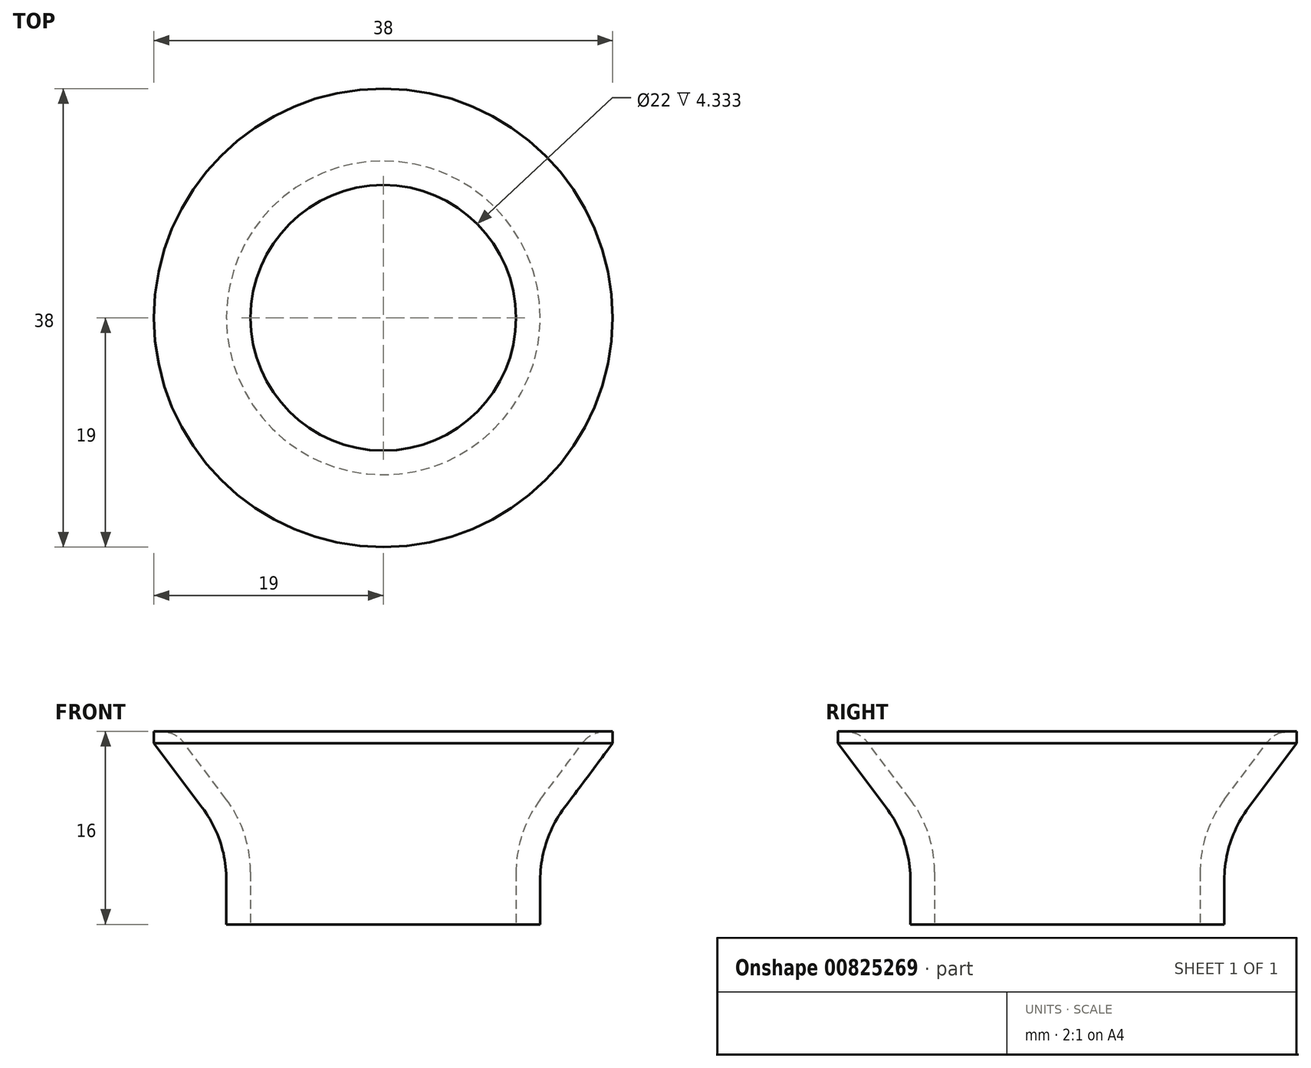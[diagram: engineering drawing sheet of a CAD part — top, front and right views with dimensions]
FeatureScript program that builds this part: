
annotation { "Feature Type Name" : "Feature", "Feature Type Description" : "" }
export const myFeature = defineFeature(function(context is Context, id is Id, definition is map)
    precondition{}
    {
        {
            var Q0;
            Q0=qCreatedBy(makeId("Top.planeOp"),FACE);
            var sketch = newSketch(context, id + "F0", { "sketchPlane" : qUnion([Q0])});
            skCircle(sketch, "E0", {"center": v(0, 0) * mm, "radius": 13 * mm});
            skSolve(sketch);
        }
        {
            var Q0;
            Q0=qCreatedBy(makeId("Top.planeOp"),FACE);
            cPlane(context, id + "F1", {"entities" : qUnion([Q0]), "cplaneType" : CPlaneType.OFFSET, "offset" : 15 * mm, "width" : 150 * mm, "height" : 150 * mm});
        }
        {
            var Q0;
            Q0=qCreatedBy(id+"F1.planeOp",FACE);
            var sketch = newSketch(context, id + "F2", { "sketchPlane" : qUnion([Q0])});
            skCircle(sketch, "E1", {"center": v(0, 0) * mm, "radius": 19 * mm});
            skSolve(sketch);
        }
        {
            var Q0;
            Q0=makeQuery(id+"F0.imprint","IMPRINT",FACE,{"disambiguationData":[TD([[makeQuery(id+"F0.imprint","IMPRINT",EDGE,{"derivedFrom":sQuery(id+"F0.wireOp",EDGE,"E0")}),1.0]])]});
            extrude(context, id + "F3", {"entities" : qUnion([Q0]), "depth" : 7 * mm, "offsetDistance" : 25 * mm});
        }
        {
            var Q0;
            Q0=makeQuery(id+"F2.imprint","IMPRINT",FACE,{"disambiguationData":[TD([[makeQuery(id+"F2.imprint","IMPRINT",EDGE,{"derivedFrom":sQuery(id+"F2.wireOp",EDGE,"E1")}),1.0]])]});
            extrude(context, id + "F4", {"entities" : qUnion([Q0]), "depth" : 1 * mm, "offsetDistance" : 25 * mm});
        }
        {
            var Q0;
            Q0=makeQuery(id+"F3.opExtrude","CAP_FACE",FACE,{"disambiguationData":[OSD([sQuery(id+"F0.wireOp",EDGE,"E0")])],"isStart":false});
            var Q1;
            Q1=makeQuery(id+"F4.opExtrude","CAP_FACE",FACE,{"disambiguationData":[OSD([sQuery(id+"F2.wireOp",EDGE,"E1")])],"isStart":true});
            loft(context, id + "F5", {"operationType" : NewBodyOperationType.ADD, "sheetProfilesArray" : [{ "sheetProfileEntities" : qUnion([Q0]) }, { "sheetProfileEntities" : qUnion([Q1]) }]});
        }
        {
            var Q0;
            Q0=makeQuery(id+"F4.opExtrude","CAP_FACE",FACE,{"disambiguationData":[OSD([sQuery(id+"F2.wireOp",EDGE,"E1")])],"isStart":false});
            var Q1;
            Q1=makeQuery(id+"F3.opExtrude","CAP_FACE",FACE,{"disambiguationData":[OSD([sQuery(id+"F0.wireOp",EDGE,"E0")])],"isStart":true});
            shell(context, id + "F6", {"entities" : qUnion([Q0, Q1]), "thickness" : 2 * mm});
        }
        {
            var Q0;
            {var subQ0=sQuery(id+"F0.wireOp",EDGE,"E0");Q0=makeQuery(id+"F5.boolean.opBoolean","MERGE",EDGE,{"derivedFrom":[makeQuery(id+"F3.opExtrude","CAP_EDGE",EDGE,{"disambiguationData":[OSD([subQ0])],"isStart":false}),makeQuery(id+"F5.opLoft","MID_CAP_EDGE",EDGE,{"disambiguationData":[OSD([subQ0])],"capPos":0.0})]});}
            fillet(context, id + "F7", {"entities" : qUnion([Q0]), "radius" : 10 * mm, "tangentPropagation" : true, "allowEdgeOverflow" : false});
        }
        {
            var Q0;
            {var subQ0=sQuery(id+"F2.wireOp",EDGE,"E1");Q0=makeQuery(id+"F6.opShell","OFFSET_EDGE",EDGE,{"disambiguationData":[OSD([subQ0]),TDD([makeQuery(id+"F4.opExtrude","CAP_EDGE",EDGE,{"disambiguationData":[OSD([subQ0])],"isStart":false})])]});}
            fillet(context, id + "F8", {"entities" : qUnion([Q0]), "radius" : 5 * mm, "tangentPropagation" : true, "allowEdgeOverflow" : false});
        }
        {
            var Q0;
            {var subQ0=sQuery(id+"F0.wireOp",EDGE,"E0");Q0=makeQuery(id+"F6.opShell","OFFSET_EDGE",EDGE,{"disambiguationData":[OSD([subQ0]),TDD([makeQuery(id+"F5.boolean.opBoolean","MERGE",EDGE,{"derivedFrom":[makeQuery(id+"F3.opExtrude","CAP_EDGE",EDGE,{"disambiguationData":[OSD([subQ0])],"isStart":false}),makeQuery(id+"F5.opLoft","MID_CAP_EDGE",EDGE,{"disambiguationData":[OSD([subQ0])],"capPos":0.0})]})])]});}
            fillet(context, id + "F9", {"entities" : qUnion([Q0]), "radius" : 10 * mm, "tangentPropagation" : true, "allowEdgeOverflow" : false});
        }
        {
            var Q0;
            {var subQ0=sQuery(id+"F2.wireOp",EDGE,"E1");Q0=makeQuery(id+"F8.opFillet","BLEND_EDGE",EDGE,{"blendedFrom":[makeQuery(id+"F6.opShell","OFFSET_EDGE",EDGE,{"disambiguationData":[OSD([subQ0]),TDD([makeQuery(id+"F4.opExtrude","CAP_EDGE",EDGE,{"disambiguationData":[OSD([subQ0])],"isStart":false})])]}),makeQuery(id+"F6.opShell","OFFSET_FACE",FACE,{"disambiguationData":[OSD([sQuery(id+"F0.wireOp",EDGE,"E0"),subQ0])]})],"blendedInto":[makeQuery(id+"F6.opShell","OFFSET_FACE",FACE,{"disambiguationData":[OSD([sQuery(id+"F0.wireOp",EDGE,"E0"),subQ0])]})]});}
            fillet(context, id + "F10", {"entities" : qUnion([Q0]), "radius" : 2 * mm, "tangentPropagation" : true, "allowEdgeOverflow" : false});
        }
    });
